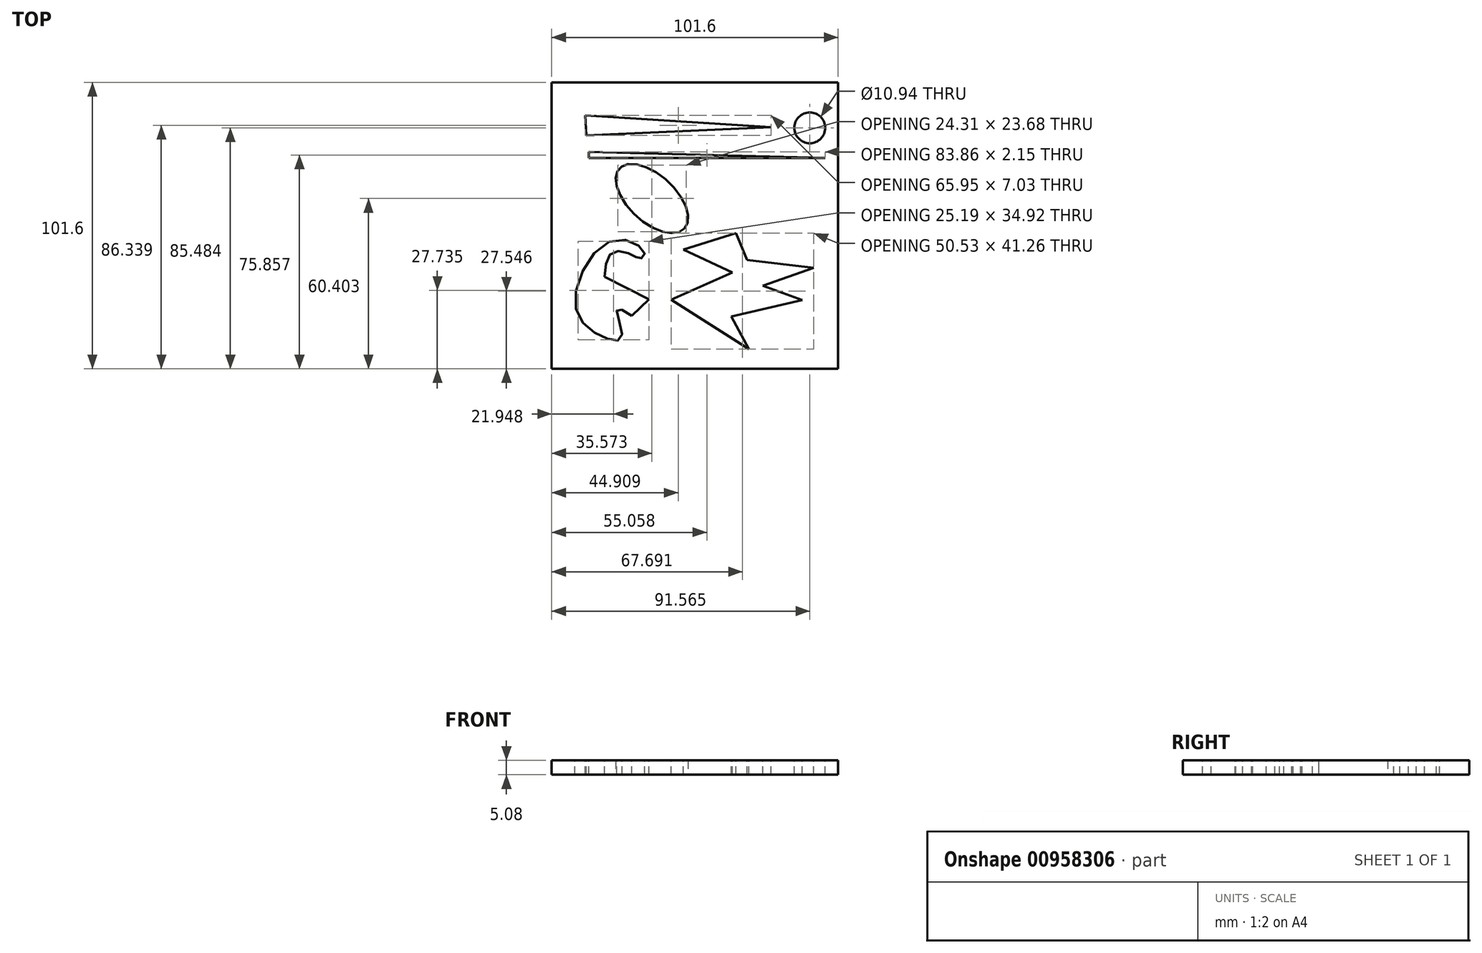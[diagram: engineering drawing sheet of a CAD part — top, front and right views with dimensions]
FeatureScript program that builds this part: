
annotation { "Feature Type Name" : "Feature", "Feature Type Description" : "" }
export const myFeature = defineFeature(function(context is Context, id is Id, definition is map)
    precondition{}
    {
        {
            var Q0;
            Q0=qCreatedBy(makeId("Top.planeOp"),FACE);
            var sketch = newSketch(context, id + "F0", { "sketchPlane" : qUnion([Q0])});
            skLineSegment(sketch, "E0.bottom", {"start": v(-50.8, 50.8) * mm, "end": v(50.8, 50.8) * mm});
            skLineSegment(sketch, "E0.top", {"start": v(-50.8, -50.8) * mm, "end": v(50.8, -50.8) * mm});
            skLineSegment(sketch, "E0.left", {"start": v(-50.8, 50.8) * mm, "end": v(-50.8, -50.8) * mm});
            skLineSegment(sketch, "E0.right", {"start": v(50.8, 50.8) * mm, "end": v(50.8, -50.8) * mm});
            skPoint(sketch, "E0.middle", {"position": v(0, 0) * mm});
            skSolve(sketch);
        }
        {
            var Q0;
            Q0=makeQuery(id+"F0.imprint","IMPRINT",FACE,{"disambiguationData":[TD([[makeQuery(id+"F0.imprint","IMPRINT",EDGE,{"derivedFrom":sQuery(id+"F0.wireOp",EDGE,"E0.bottom")}),-1.0]])]});
            extrude(context, id + "F1", {"entities" : qUnion([Q0]), "depth" : 5.08 * mm, "offsetDistance" : 25.4 * mm});
        }
        {
            var Q0;
            Q0=makeQuery(id+"F1.opExtrude","CAP_FACE",FACE,{"disambiguationData":[OSD([sQuery(id+"F0.wireOp",EDGE,"E0.bottom"),sQuery(id+"F0.wireOp",EDGE,"E0.top"),sQuery(id+"F0.wireOp",EDGE,"E0.left"),sQuery(id+"F0.wireOp",EDGE,"E0.right")])],"isStart":false});
            var sketch = newSketch(context, id + "F2", { "sketchPlane" : qUnion([Q0])});
            skLineSegment(sketch, "E1", {"start": v(-38.86, 39.05) * mm, "end": v(27.08, 34.87) * mm});
            skLineSegment(sketch, "E2", {"start": v(27.08, 34.87) * mm, "end": v(-38.48, 32.02) * mm});
            skLineSegment(sketch, "E3", {"start": v(-38.48, 32.02) * mm, "end": v(-38.86, 39.05) * mm});
            skCircle(sketch, "E4", {"center": v(40.77, 34.68) * mm, "radius": 5.47 * mm});
            skLineSegment(sketch, "E5", {"start": v(-32.03, -18.16) * mm, "end": v(-16.26, -26.14) * mm});
            skLineSegment(sketch, "E6", {"start": v(-16.26, -26.14) * mm, "end": v(-22.33, -32.02) * mm});
            skFitSpline(sketch, "E7", {"points": [v(-22.33, -32.02) * mm, v(-27.65, -29.93) * mm, v(-25.94, -39.62) * mm, v(-32.03, -39.81) * mm, v(-42.48, -27.65) * mm, v(-28.41, -5.04) * mm, v(-17.77, -9.98) * mm, v(-19.29, -11.69) * mm, v(-22.33, -10.36) * mm, v(-29.36, -9.6) * mm, v(-32.03, -18.16) * mm], "startDerivative": vector(-90.77, 58.68) * mm, "endDerivative": vector(-8.94, -108.75) * mm});
            skLineSegment(sketch, "E8", {"start": v(18.5, -12.17) * mm, "end": v(42.15, -14.99) * mm});
            skLineSegment(sketch, "E9", {"start": v(42.15, -14.99) * mm, "end": v(24.15, -21.3) * mm});
            skLineSegment(sketch, "E10", {"start": v(24.15, -21.3) * mm, "end": v(38.12, -26.41) * mm});
            skLineSegment(sketch, "E11", {"start": v(38.12, -26.41) * mm, "end": v(13, -32.32) * mm});
            skLineSegment(sketch, "E12", {"start": v(13, -32.32) * mm, "end": v(19.18, -43.88) * mm});
            skLineSegment(sketch, "E13", {"start": v(19.18, -43.88) * mm, "end": v(-8.37, -26.28) * mm});
            skLineSegment(sketch, "E14", {"start": v(-8.37, -26.28) * mm, "end": v(13.26, -16.6) * mm});
            skLineSegment(sketch, "E15", {"start": v(13.26, -16.6) * mm, "end": v(-4.07, -8.54) * mm});
            skLineSegment(sketch, "E16", {"start": v(-4.07, -8.54) * mm, "end": v(14.6, -2.63) * mm});
            skLineSegment(sketch, "E17", {"start": v(14.6, -2.63) * mm, "end": v(18.5, -12.17) * mm});
            skLineSegment(sketch, "E18", {"start": v(-37.67, 26.13) * mm, "end": v(-37.67, 23.98) * mm});
            skLineSegment(sketch, "E19", {"start": v(-37.67, 23.98) * mm, "end": v(46.19, 23.98) * mm});
            skLineSegment(sketch, "E20", {"start": v(46.19, 23.98) * mm, "end": v(-37.67, 26.13) * mm});
            skEllipse(sketch, "E21", {"center": v(-15.23, 9.6) * mm, "majorRadius": 15.7 * mm, "minorRadius": 8.32 * mm, "majorAxis": v(0.74, -0.68)});
            skSolve(sketch);
        }
        {
            var Q0;
            Q0 = qSketchRegion(id + "F2", true);
            extrude(context, id + "F3", {"entities" : qUnion([Q0]), "operationType" : NewBodyOperationType.REMOVE, "endBound" : BoundingType.THROUGH_ALL, "oppositeDirection" : true, "depth" : 25.4 * mm, "offsetDistance" : 25.4 * mm});
        }
    });
